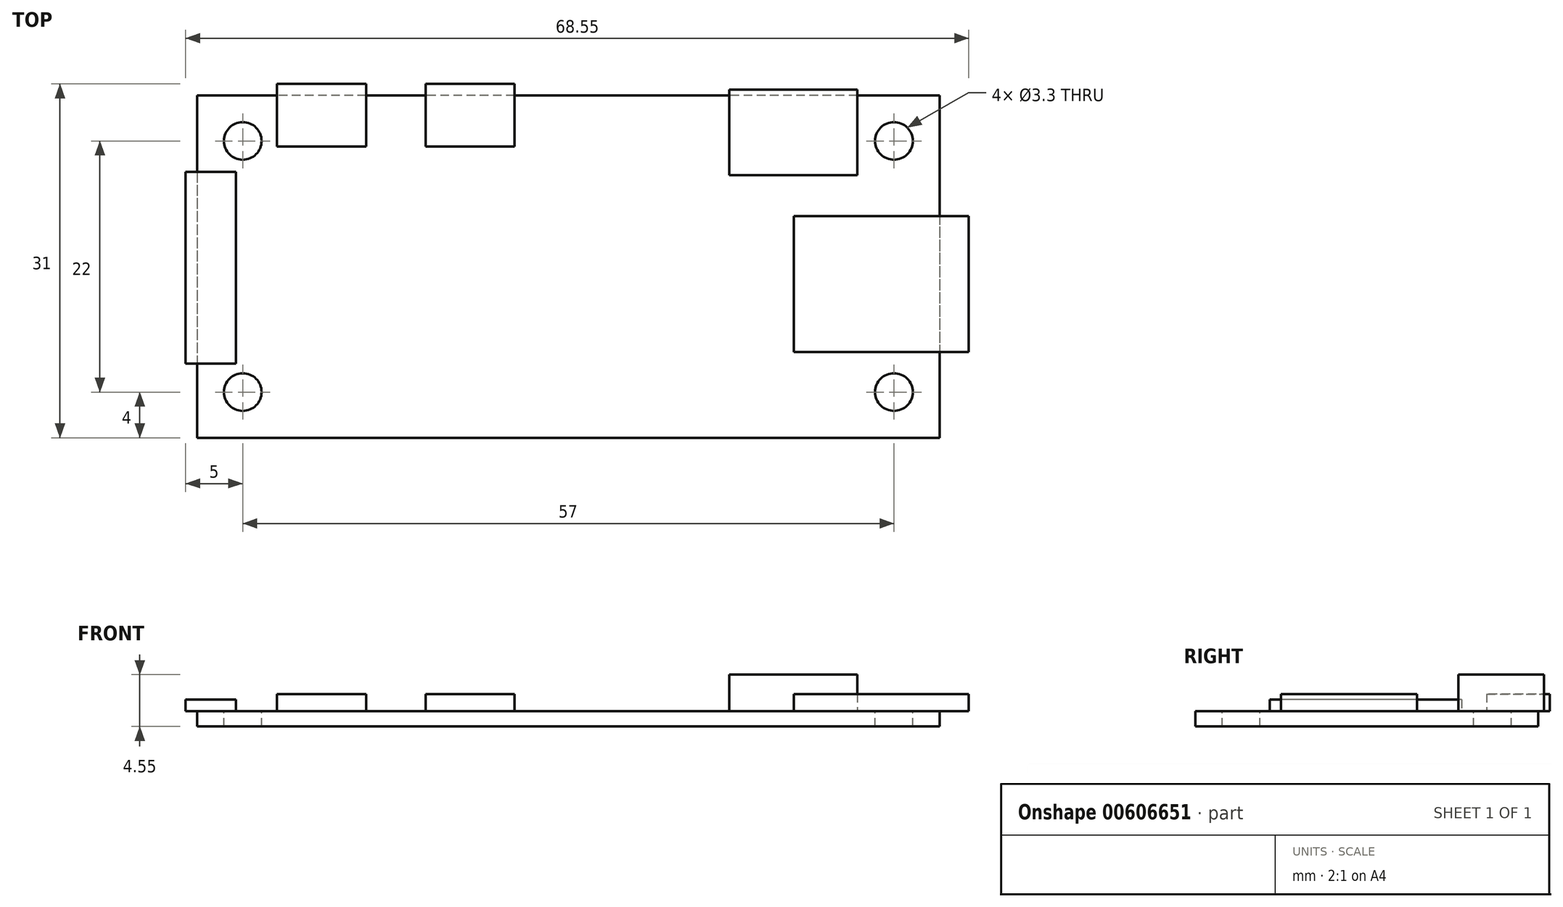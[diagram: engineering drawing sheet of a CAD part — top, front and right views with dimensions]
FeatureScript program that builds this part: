
annotation { "Feature Type Name" : "Feature", "Feature Type Description" : "" }
export const myFeature = defineFeature(function(context is Context, id is Id, definition is map)
    precondition{}
    {
        {
            var Q0;
            Q0=qCreatedBy(makeId("Top.planeOp"),FACE);
            var sketch = newSketch(context, id + "F0", { "sketchPlane" : qUnion([Q0])});
            skLineSegment(sketch, "E0.bottom", {"start": v(32.5, 15) * mm, "end": v(-32.5, 15) * mm});
            skLineSegment(sketch, "E0.top", {"start": v(32.5, -15) * mm, "end": v(-32.5, -15) * mm});
            skLineSegment(sketch, "E0.left", {"start": v(32.5, 15) * mm, "end": v(32.5, -15) * mm});
            skLineSegment(sketch, "E0.right", {"start": v(-32.5, 15) * mm, "end": v(-32.5, -15) * mm});
            skPoint(sketch, "E0.middle", {"position": v(0, 0) * mm});
            skSolve(sketch);
        }
        {
            var Q0;
            Q0=makeQuery(id+"F0.imprint","IMPRINT",FACE,{"disambiguationData":[TD([[makeQuery(id+"F0.imprint","IMPRINT",EDGE,{"derivedFrom":sQuery(id+"F0.wireOp",EDGE,"E0.bottom")}),1.0]])]});
            extrude(context, id + "F1", {"entities" : qUnion([Q0]), "depth" : 1.35 * mm, "offsetDistance" : 25 * mm});
        }
        {
            var Q0;
            Q0=makeQuery(id+"F1.opExtrude","CAP_FACE",FACE,{"disambiguationData":[OSD([sQuery(id+"F0.wireOp",EDGE,"E0.bottom"),sQuery(id+"F0.wireOp",EDGE,"E0.top"),sQuery(id+"F0.wireOp",EDGE,"E0.left"),sQuery(id+"F0.wireOp",EDGE,"E0.right")])],"isStart":false});
            var sketch = newSketch(context, id + "F2", { "sketchPlane" : qUnion([Q0])});
            skPoint(sketch, "E1", {"position": v(-28.5, 11) * mm});
            skPoint(sketch, "E2", {"position": v(-28.5, -11) * mm});
            skPoint(sketch, "E3", {"position": v(28.5, -11) * mm});
            skPoint(sketch, "E4", {"position": v(28.5, 11) * mm});
            skLineSegment(sketch, "E5.bottom", {"start": v(14.1, 15.5) * mm, "end": v(25.3, 15.5) * mm});
            skLineSegment(sketch, "E5.top", {"start": v(14.1, 8) * mm, "end": v(25.3, 8) * mm});
            skLineSegment(sketch, "E5.left", {"start": v(14.1, 15.5) * mm, "end": v(14.1, 8) * mm});
            skLineSegment(sketch, "E5.right", {"start": v(25.3, 15.5) * mm, "end": v(25.3, 8) * mm});
            skLineSegment(sketch, "E6.bottom", {"start": v(19.75, 4.4) * mm, "end": v(35.05, 4.4) * mm});
            skLineSegment(sketch, "E6.top", {"start": v(19.75, -7.5) * mm, "end": v(35.05, -7.5) * mm});
            skLineSegment(sketch, "E6.left", {"start": v(19.75, 4.4) * mm, "end": v(19.75, -7.5) * mm});
            skLineSegment(sketch, "E6.right", {"start": v(35.05, 4.4) * mm, "end": v(35.05, -7.5) * mm});
            skLineSegment(sketch, "E7.bottom", {"start": v(-25.5, 16) * mm, "end": v(-17.7, 16) * mm});
            skLineSegment(sketch, "E7.top", {"start": v(-25.5, 10.5) * mm, "end": v(-17.7, 10.5) * mm});
            skLineSegment(sketch, "E7.left", {"start": v(-25.5, 16) * mm, "end": v(-25.5, 10.5) * mm});
            skLineSegment(sketch, "E7.right", {"start": v(-17.7, 16) * mm, "end": v(-17.7, 10.5) * mm});
            skLineSegment(sketch, "E8.bottom", {"start": v(-12.5, 10.5) * mm, "end": v(-4.7, 10.5) * mm});
            skLineSegment(sketch, "E8.top", {"start": v(-12.5, 16) * mm, "end": v(-4.7, 16) * mm});
            skLineSegment(sketch, "E8.left", {"start": v(-12.5, 10.5) * mm, "end": v(-12.5, 16) * mm});
            skLineSegment(sketch, "E8.right", {"start": v(-4.7, 10.5) * mm, "end": v(-4.7, 16) * mm});
            skLineSegment(sketch, "E9.bottom", {"start": v(-33.5, 8.3) * mm, "end": v(-29.1, 8.3) * mm});
            skLineSegment(sketch, "E9.top", {"start": v(-33.5, -8.5) * mm, "end": v(-29.1, -8.5) * mm});
            skLineSegment(sketch, "E9.left", {"start": v(-33.5, 8.3) * mm, "end": v(-33.5, -8.5) * mm});
            skLineSegment(sketch, "E9.right", {"start": v(-29.1, 8.3) * mm, "end": v(-29.1, -8.5) * mm});
            skSolve(sketch);
        }
        {
            var Q0;
            {var subQ0=sQuery(id+"F2.wireOp",EDGE,"E6.left");Q0=makeQuery(id+"F2.imprint","IMPRINT",FACE,{"disambiguationData":[TD([[makeQuery(id+"F2.imprint","IMPRINT",EDGE,{"derivedFrom":subQ0}),1.0]])]});}
            var Q1;
            {var subQ0=sQuery(id+"F2.wireOp",EDGE,"E6.right");Q1=makeQuery(id+"F2.imprint","IMPRINT",FACE,{"disambiguationData":[TD([[makeQuery(id+"F2.imprint","IMPRINT",EDGE,{"derivedFrom":subQ0}),-1.0]])]});}
            extrude(context, id + "F3", {"entities" : qUnion([Q0, Q1]), "operationType" : NewBodyOperationType.ADD, "depth" : 1.5 * mm, "offsetDistance" : 25 * mm});
        }
        {
            var Q0;
            {var subQ0=sQuery(id+"F2.wireOp",EDGE,"E7.top");Q0=makeQuery(id+"F2.imprint","IMPRINT",FACE,{"disambiguationData":[TD([[makeQuery(id+"F2.imprint","IMPRINT",EDGE,{"derivedFrom":subQ0}),1.0]])]});}
            var Q1;
            {var subQ0=sQuery(id+"F2.wireOp",EDGE,"E8.top");Q1=makeQuery(id+"F2.imprint","IMPRINT",FACE,{"disambiguationData":[TD([[makeQuery(id+"F2.imprint","IMPRINT",EDGE,{"derivedFrom":subQ0}),-1.0]])]});}
            var Q2;
            {var subQ0=sQuery(id+"F2.wireOp",EDGE,"E8.bottom");Q2=makeQuery(id+"F2.imprint","IMPRINT",FACE,{"disambiguationData":[TD([[makeQuery(id+"F2.imprint","IMPRINT",EDGE,{"derivedFrom":subQ0}),1.0]])]});}
            var Q3;
            {var subQ0=sQuery(id+"F2.wireOp",EDGE,"E7.bottom");Q3=makeQuery(id+"F2.imprint","IMPRINT",FACE,{"disambiguationData":[TD([[makeQuery(id+"F2.imprint","IMPRINT",EDGE,{"derivedFrom":subQ0}),-1.0]])]});}
            extrude(context, id + "F4", {"entities" : qUnion([Q0, Q1, Q2, Q3]), "operationType" : NewBodyOperationType.ADD, "depth" : 1.5 * mm, "offsetDistance" : 25 * mm});
        }
        {
            var Q0;
            {var subQ0=sQuery(id+"F2.wireOp",EDGE,"E9.left");Q0=makeQuery(id+"F2.imprint","IMPRINT",FACE,{"disambiguationData":[TD([[makeQuery(id+"F2.imprint","IMPRINT",EDGE,{"derivedFrom":subQ0}),1.0]])]});}
            var Q1;
            {var subQ0=sQuery(id+"F2.wireOp",EDGE,"E9.right");Q1=makeQuery(id+"F2.imprint","IMPRINT",FACE,{"disambiguationData":[TD([[makeQuery(id+"F2.imprint","IMPRINT",EDGE,{"derivedFrom":subQ0}),-1.0]])]});}
            extrude(context, id + "F5", {"entities" : qUnion([Q0, Q1]), "operationType" : NewBodyOperationType.ADD, "depth" : 1 * mm, "offsetDistance" : 25 * mm});
        }
        {
            var Q0;
            {var subQ0=sQuery(id+"F2.wireOp",EDGE,"E5.bottom");Q0=makeQuery(id+"F2.imprint","IMPRINT",FACE,{"disambiguationData":[TD([[makeQuery(id+"F2.imprint","IMPRINT",EDGE,{"derivedFrom":subQ0}),-1.0]])]});}
            var Q1;
            {var subQ0=sQuery(id+"F2.wireOp",EDGE,"E5.top");Q1=makeQuery(id+"F2.imprint","IMPRINT",FACE,{"disambiguationData":[TD([[makeQuery(id+"F2.imprint","IMPRINT",EDGE,{"derivedFrom":subQ0}),1.0]])]});}
            extrude(context, id + "F6", {"entities" : qUnion([Q0, Q1]), "operationType" : NewBodyOperationType.ADD, "depth" : 3.2 * mm, "offsetDistance" : 25 * mm});
        }
        {
            var Q0;
            Q0=sQuery(id+"F2.wireOp",VERTEX,"E4");
            var Q1;
            Q1=sQuery(id+"F2.wireOp",VERTEX,"E3");
            var Q2;
            Q2=sQuery(id+"F2.wireOp",VERTEX,"E1");
            var Q3;
            Q3=sQuery(id+"F2.wireOp",VERTEX,"E2");
            var Q4;
            Q4=makeQuery(id+"F1.opExtrude","SWEPT_BODY",BODY,{"disambiguationData":[OSD([sQuery(id+"F0.wireOp",EDGE,"E0.bottom"),sQuery(id+"F0.wireOp",EDGE,"E0.top"),sQuery(id+"F0.wireOp",EDGE,"E0.left"),sQuery(id+"F0.wireOp",EDGE,"E0.right")])]});
            hole(context, id + "F7", {"style" : HoleStyle.SIMPLE, "endStyle" : HoleEndStyle.BLIND, "standardTappedOrClearance" : lookupTablePath({ "standard" : "ISO", "fit" : "Normal", "size" : "M3", "type" : "Clearance" }), "standardBlindInLast" : lookupTablePath({ "fit" : "Standard", "standard" : "ISO", "size" : "M3", "type" : "Clearance" }), "holeDiameter" : 3.3 * mm, "majorDiameter" : 5 * mm, "holeDepth" : 9 * mm, "isTappedThrough" : true, "tappedDepth" : 3.5 * mm, "tapClearance" : 3, "locations" : qUnion([Q0, Q1, Q2, Q3]), "scope" : qUnion([Q4])});
        }
    });
